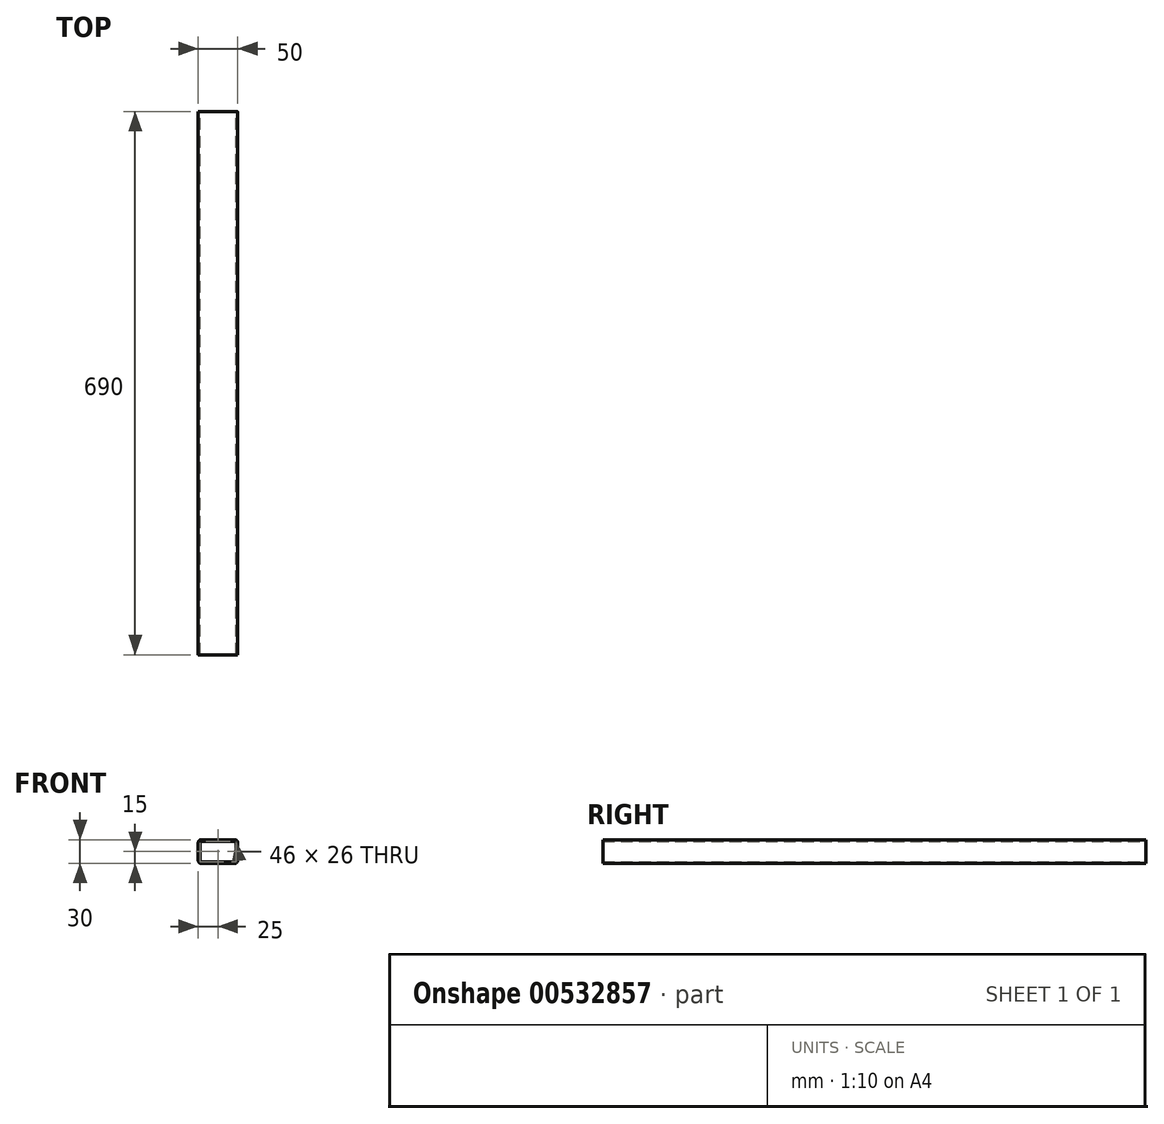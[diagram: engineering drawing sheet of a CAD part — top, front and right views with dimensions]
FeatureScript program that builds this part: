
annotation { "Feature Type Name" : "Feature", "Feature Type Description" : "" }
export const myFeature = defineFeature(function(context is Context, id is Id, definition is map)
    precondition{}
    {
        {
            var Q0;
            Q0=qCreatedBy(makeId("Front.planeOp"),FACE);
            var sketch = newSketch(context, id + "F0", { "sketchPlane" : qUnion([Q0])});
            skLineSegment(sketch, "E0.bottom", {"start": v(23, -13) * mm, "end": v(-23, -13) * mm});
            skLineSegment(sketch, "E0.top", {"start": v(23, 13) * mm, "end": v(-23, 13) * mm});
            skLineSegment(sketch, "E0.left", {"start": v(23, -13) * mm, "end": v(23, 13) * mm});
            skLineSegment(sketch, "E0.right", {"start": v(-23, -13) * mm, "end": v(-23, 13) * mm});
            skPoint(sketch, "E0.middle", {"position": v(0, 0) * mm});
            skLineSegment(sketch, "E1.bottom", {"start": v(21.5, -15) * mm, "end": v(-21.5, -15) * mm});
            skLineSegment(sketch, "E1.top", {"start": v(21.5, 15) * mm, "end": v(-21.5, 15) * mm});
            skLineSegment(sketch, "E1.left", {"start": v(25, -11.5) * mm, "end": v(25, 11.5) * mm});
            skLineSegment(sketch, "E1.right", {"start": v(-25, -11.5) * mm, "end": v(-25, 11.5) * mm});
            skPoint(sketch, "E2.visualSharp", {"position": v(-25, 15) * mm});
            skArc(sketch, "E2.filletArc", {"start": v(-21.5, 15) * mm, "mid": v(-23.97, 13.97) * mm, "end": v(-25, 11.5) * mm});
            skPoint(sketch, "E3.visualSharp", {"position": v(25, 15) * mm});
            skArc(sketch, "E3.filletArc", {"start": v(25, 11.5) * mm, "mid": v(23.97, 13.97) * mm, "end": v(21.5, 15) * mm});
            skPoint(sketch, "E4.visualSharp", {"position": v(25, -15) * mm});
            skArc(sketch, "E4.filletArc", {"start": v(21.5, -15) * mm, "mid": v(23.97, -13.97) * mm, "end": v(25, -11.5) * mm});
            skPoint(sketch, "E5.visualSharp", {"position": v(-25, -15) * mm});
            skArc(sketch, "E5.filletArc", {"start": v(-25, -11.5) * mm, "mid": v(-23.97, -13.97) * mm, "end": v(-21.5, -15) * mm});
            skSolve(sketch);
        }
        {
            var Q0;
            Q0=makeQuery(id+"F0.imprint","IMPRINT",FACE,{"disambiguationData":[TD([[makeQuery(id+"F0.imprint","IMPRINT",EDGE,{"derivedFrom":sQuery(id+"F0.wireOp",EDGE,"E0.bottom")}),1.0]])]});
            extrude(context, id + "F1", {"entities" : qUnion([Q0]), "depth" : 690 * mm, "offsetDistance" : 25 * mm});
        }
    });
